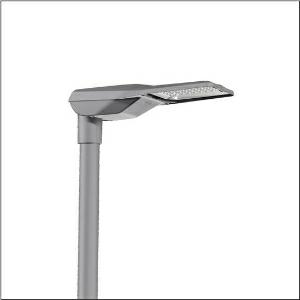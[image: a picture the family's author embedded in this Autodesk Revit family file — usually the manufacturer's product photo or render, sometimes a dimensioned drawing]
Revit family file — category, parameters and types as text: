
# Revit family: streetlight_sl_21_iq_mini___st0_8a_5xe2c41g08hb_fab9
name_source: partatom
category: Lighting Fixtures
units: mm (PartAtom-declared; Revit-internal decimal feet)

## family parameters
Cut with Voids When Loaded = No
Host = Face
Light Source = No
Part Type = Normal
Room Calculation Point = No
Round Connector Dimension = Use Diameter
Shared = No

## types (1)
- --- (1 x LED, 9860 lm, 70.9 W, 4000K)
    Apparent Load = 71 VA
    CIE Flux Codes = 38 75 97 100 100
    Color Rendering = 70
    Color Temperature = 4000K
    Default Elevation = 1800 mm
    Description = Streetlight SL 21 mini, mast luminaire, primary light control with lens, of PMMA, primary optical cover: cover, of toughened safety glass, transparent, light distribution: ST0.8a, light emission: direct distribution, primary light characteristic: asymmetric, installation type: post-top, side-entry, LED, High Power LED, rated luminous flux: 9.860lm, luminous efficacy: 139lm/W, light colour: 740, colour temperature: 4000K, control gear: ECG iQ, control: Street-Remote, Auto-Match, Temp-Guard, Lumen-Switch, Night-Set, Smart-Wire, Light-Fading, Desk-Remote (wireless, voltage-free reading and setting of iQ features in the workshop via application-optimized NFC function/RFID function), optimised constant luminous flux control (CLO 2.0), mains connection: 220..240V, AC, 50/60Hz, start of lifetime: 71W, end of lifetime: 75W, reduction: 31W, luminaire housing, of diecast aluminium, powder-coated, Siteco® metallic grey (DB 702S), corrosivity category C5 according to DIN EN ISO 12944, length: 628mm, width: 235mm, height: 110mm, spigot size: 60/76mm (post-top) and 42/60/76mm (side-entry), mast flange for spigot size: 42mm: 5XC10008XM4, 60mm: 5XC10008XM2, 76/60mm: 5XC10108XM1, protection rating (complete): IP66, insulation class (complete): insulation class II (safety insulation), certification: CE, ENEC, VDE, impact resistance: IK09, permissible operating ambient temperature for outdoor applications: -40..+50°C, standard-compliant lighting for roads and squares, packaging unit: 1 piece

Light Distribution: ST0.8a
    Height = 110 mm
    Lamp = 1 x LED
    Lamp Light Flux = 9860 lm
    Lamp Power = 70.9 W
    Lamp count = 1
    Length = 625 mm
    Luminous efficacy = 139 lm/W
    Manufacturer = Siteco
    ModVariant = No
    Model = 5XE2C41G08HB
    Number of Poles = 1
    OnlyDefault = Yes
    Power Factor = 1
    Product Name = Streetlight SL 21 iQ mini | ST0.8a
    Product group = mast luminaire | pylon top
    ProductGroupID = 6100
    Protection Class = Protection class II
    Protection Degree = IP 66
    RLX_Detail_Level = 1
    RlxData = <blob elided: 92181 chars, md5=626f32b6>
    Socket = socket
    Standby Power = 0 W
    System Light Flux = 9860 lm
    System Power = 71 W
    Type Comments = factory setting: luminous flux: 100 % | dim-lin: 254 | 711 mA
    Type Image = l_1003519.jpg
    URL = http://relux.com
    VarID = @adj_068581
    Voltage = 0 V
    Weight = 0.00 kg
    Width = 234 mm

## geometry (parser evidence)
native form markers: Blend x4, Sweep x13
no freeform markers — native parametric forms only
